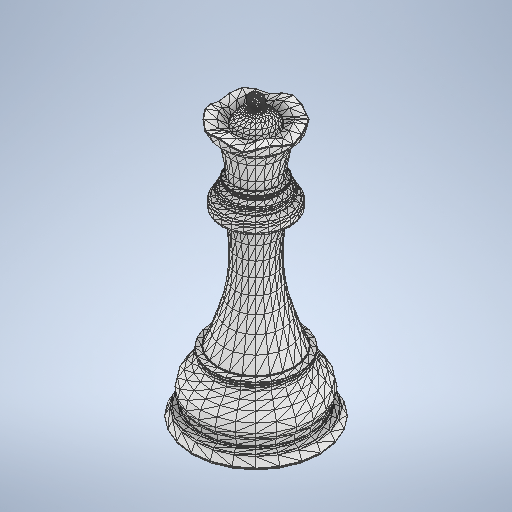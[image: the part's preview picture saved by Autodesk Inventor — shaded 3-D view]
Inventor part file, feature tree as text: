
AUTODESK INVENTOR PART (.ipt)
format: ipt  version: 2025.2 (Build 292293000, 293)  size: 7,672,832 bytes
history: native  units: mm
features: other x4, move_body x3, direct_edit x1, extrude x1, chamfer x1, sketch x1
ambient origin geometry x8: Origin, YZ Plane, XZ Plane, XY Plane, X Axis, Y Axis, Z Axis, Center Point
bodies: Body1 (feature_tree)
feature tree (11):
  other  "ChessSet v2.ipt"
  other  "Work Axis1"
  move_body  "Move Body1"
  direct_edit  "Direct Edit1"
  move_body  "Move Body2"
  extrude  "Extrusion1"  TaperAngle=90.0deg  [1 undecoded]
  chamfer  "Chamfer1"  [1 undecoded]
  other  "Solid6::ChessSet v2.ipt"
  other  "TaggingFeature1"
  sketch  "Sketch1"  dims[d0=10.0mm d1=90.0deg d2=-166.900014mm d3=0.0mm d4=-5.371734mm d5=-8.5765mm d6=0.0mm d7=0.0mm d8=10.2mm d9=2.2mm d10=0.0mm d11=0.5mm d12=2.0mm d13=45.0deg]
  move_body  "Move1"
note: 2 required parameter values undecoded (feature->parameter linkage not recoverable at this tier; creation-order binding heuristic only, values carry confidence <= 0.55)
